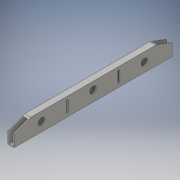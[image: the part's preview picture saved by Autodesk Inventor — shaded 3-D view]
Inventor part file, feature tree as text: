
AUTODESK INVENTOR PART (.ipt)
format: ipt  version: 2016 (Build 200138000, 138)  size: 149,504 bytes
history: native  units: in
note: dims shown in document units (in); Inventor stores cm internally (conversion verified against a paired STEP export)
features: sketch x1, projected_geometry x1, imported_body x1
ambient origin geometry x8: Origin, YZ Plane, XZ Plane, XY Plane, X Axis, Y Axis, Z Axis, Center Point
bodies: Solid1 (feature_tree)
feature tree (3):
  sketch  "Sketch1"  dims[d0=1.25in d1=1.5in d3=90.0deg d4=0.6875in d5=0.9375in]
  projected_geometry  "Projected Loop1"
  imported_body  "Base1"
